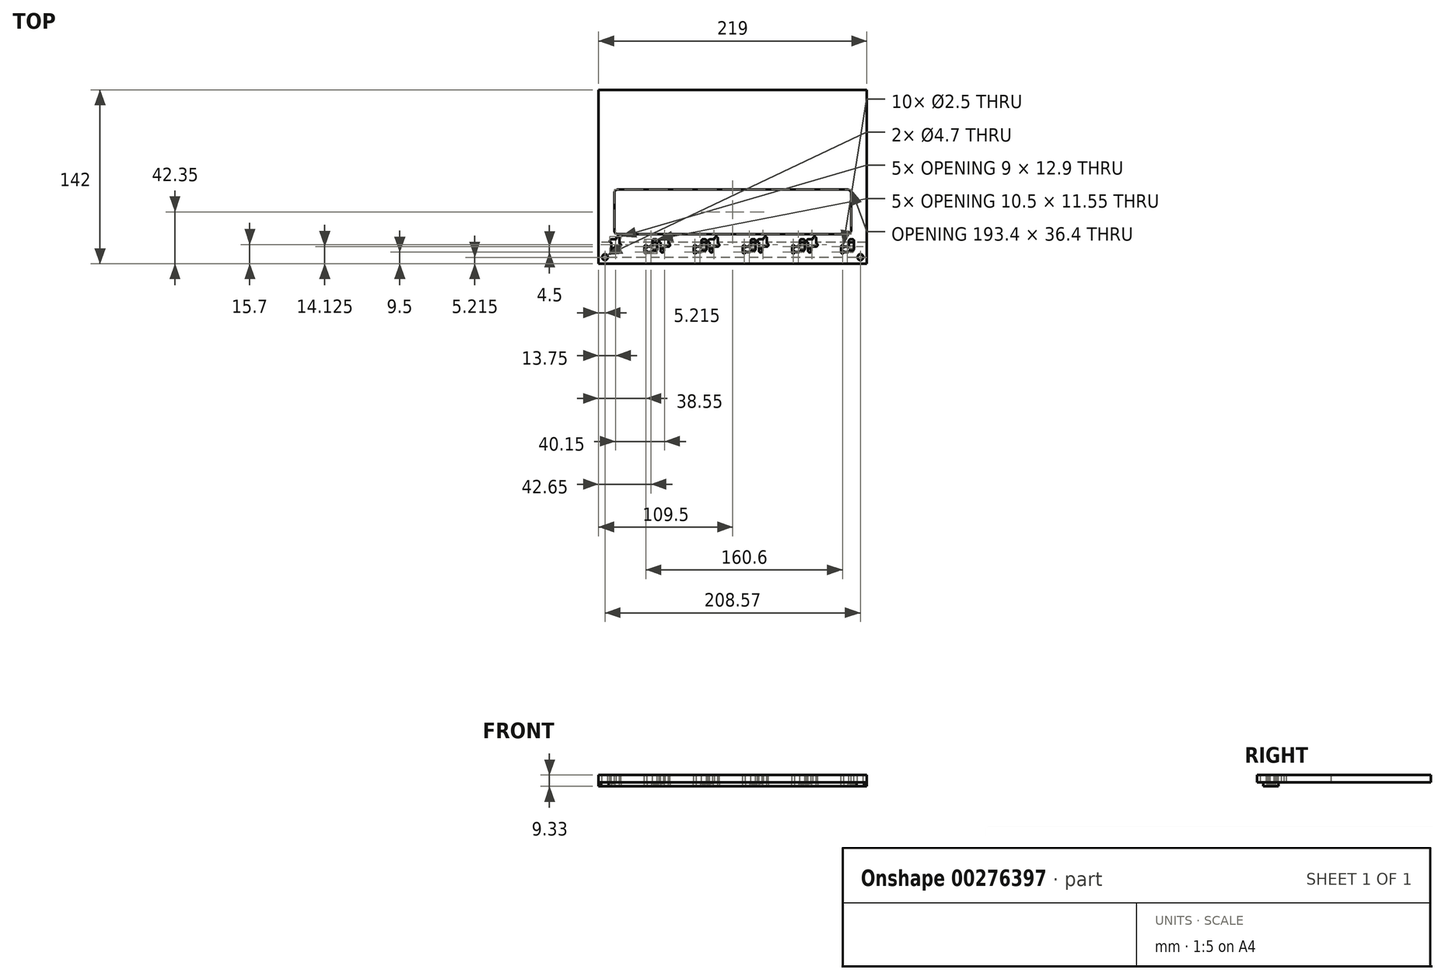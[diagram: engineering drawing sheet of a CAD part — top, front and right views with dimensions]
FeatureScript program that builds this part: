
annotation { "Feature Type Name" : "Feature", "Feature Type Description" : "" }
export const myFeature = defineFeature(function(context is Context, id is Id, definition is map)
    precondition{}
    {
        {
            var Q0;
            Q0=qCreatedBy(makeId("Top.planeOp"),FACE);
            var sketch = newSketch(context, id + "F0", { "sketchPlane" : qUnion([Q0])});
            skLineSegment(sketch, "E0.bottom", {"start": v(0, 0) * mm, "end": v(219, 0) * mm});
            skLineSegment(sketch, "E0.top", {"start": v(0, 142) * mm, "end": v(219, 142) * mm});
            skLineSegment(sketch, "E0.left", {"start": v(0, 0) * mm, "end": v(0, 142) * mm});
            skLineSegment(sketch, "E0.right", {"start": v(219, 0) * mm, "end": v(219, 142) * mm});
            skSolve(sketch);
        }
        {
            var Q0;
            Q0 = qSketchRegion(id + "F0", true);
            extrude(context, id + "F1", {"entities" : qUnion([Q0]), "depth" : 6.15 * mm});
        }
        {
            var Q0;
            Q0=makeQuery(id+"F1.opExtrude","CAP_FACE",FACE,{"disambiguationData":[OSD([sQuery(id+"F0.wireOp",EDGE,"E0.bottom"),sQuery(id+"F0.wireOp",EDGE,"E0.top"),sQuery(id+"F0.wireOp",EDGE,"E0.left"),sQuery(id+"F0.wireOp",EDGE,"E0.right")])],"isStart":false});
            var sketch = newSketch(context, id + "F2", { "sketchPlane" : qUnion([Q0])});
            skLineSegment(sketch, "E1.bottom", {"start": v(207.5, 19.9) * mm, "end": v(205.5, 19.9) * mm});
            skLineSegment(sketch, "E1.top", {"start": v(207.5, 10.8) * mm, "end": v(204.5, 10.8) * mm});
            skLineSegment(sketch, "E1.left", {"start": v(208.5, 18.9) * mm, "end": v(208.5, 11.8) * mm});
            skLineSegment(sketch, "E1.right", {"start": v(204.5, 18.9) * mm, "end": v(204.5, 14.8) * mm});
            skLineSegment(sketch, "E2.bottom", {"start": v(203.7, 14) * mm, "end": v(200.3, 14) * mm});
            skLineSegment(sketch, "E2.top", {"start": v(203.5, 9.5) * mm, "end": v(200.3, 9.5) * mm});
            skLineSegment(sketch, "E2.left", {"start": v(204.5, 10.8) * mm, "end": v(204.5, 10.5) * mm});
            skLineSegment(sketch, "E2.right", {"start": v(198, 14) * mm, "end": v(198, 9.5) * mm});
            skArc(sketch, "E3", {"start": v(200.3, 14) * mm, "mid": v(199.15, 15.15) * mm, "end": v(198, 14) * mm});
            skArc(sketch, "E4", {"start": v(198, 9.5) * mm, "mid": v(199.15, 8.35) * mm, "end": v(200.3, 9.5) * mm});
            skPoint(sketch, "E5.visualSharp", {"position": v(204.5, 19.9) * mm});
            skArc(sketch, "E5.filletArc", {"start": v(205.5, 19.9) * mm, "mid": v(204.8, 19.6) * mm, "end": v(204.5, 18.9) * mm});
            skPoint(sketch, "E6.visualSharp", {"position": v(208.5, 19.9) * mm});
            skArc(sketch, "E6.filletArc", {"start": v(208.5, 18.9) * mm, "mid": v(208.2, 19.6) * mm, "end": v(207.5, 19.9) * mm});
            skPoint(sketch, "E7.visualSharp", {"position": v(208.5, 10.8) * mm});
            skArc(sketch, "E7.filletArc", {"start": v(207.5, 10.8) * mm, "mid": v(208.2, 11.1) * mm, "end": v(208.5, 11.8) * mm});
            skPoint(sketch, "E8.visualSharp", {"position": v(204.5, 9.5) * mm});
            skArc(sketch, "E8.filletArc", {"start": v(203.5, 9.5) * mm, "mid": v(204.2, 9.8) * mm, "end": v(204.5, 10.5) * mm});
            skPoint(sketch, "E9.1.0.0", {"position": v(168.35, 10.8) * mm});
            skPoint(sketch, "E9.1.0.1", {"position": v(164.35, 19.9) * mm});
            skLineSegment(sketch, "E9.1.0.2", {"start": v(168.35, 18.9) * mm, "end": v(168.35, 11.8) * mm});
            skPoint(sketch, "E9.1.0.3", {"position": v(168.35, 19.9) * mm});
            skPoint(sketch, "E9.1.0.4", {"position": v(164.35, 9.5) * mm});
            skLineSegment(sketch, "E9.1.0.5", {"start": v(164.35, 18.9) * mm, "end": v(164.35, 14.8) * mm});
            skLineSegment(sketch, "E9.1.0.6", {"start": v(157.85, 14) * mm, "end": v(157.85, 9.5) * mm});
            skLineSegment(sketch, "E9.1.0.7", {"start": v(167.35, 10.8) * mm, "end": v(164.35, 10.8) * mm});
            skLineSegment(sketch, "E9.1.0.8", {"start": v(163.55, 14) * mm, "end": v(160.15, 14) * mm});
            skArc(sketch, "E9.1.0.9", {"start": v(167.35, 10.8) * mm, "mid": v(168.06, 11.1) * mm, "end": v(168.35, 11.8) * mm});
            skArc(sketch, "E9.1.0.10", {"start": v(163.35, 9.5) * mm, "mid": v(164.06, 9.8) * mm, "end": v(164.35, 10.5) * mm});
            skLineSegment(sketch, "E9.1.0.11", {"start": v(167.35, 19.9) * mm, "end": v(165.35, 19.9) * mm});
            skArc(sketch, "E9.1.0.12", {"start": v(165.35, 19.9) * mm, "mid": v(164.64, 19.6) * mm, "end": v(164.35, 18.9) * mm});
            skArc(sketch, "E9.1.0.13", {"start": v(168.35, 18.9) * mm, "mid": v(168.06, 19.6) * mm, "end": v(167.35, 19.9) * mm});
            skArc(sketch, "E9.1.0.14", {"start": v(160.15, 14) * mm, "mid": v(159, 15.15) * mm, "end": v(157.85, 14) * mm});
            skLineSegment(sketch, "E9.1.0.15", {"start": v(163.35, 9.5) * mm, "end": v(160.15, 9.5) * mm});
            skArc(sketch, "E9.1.0.16", {"start": v(157.85, 9.5) * mm, "mid": v(159, 8.35) * mm, "end": v(160.15, 9.5) * mm});
            skPoint(sketch, "E9.2.0.0", {"position": v(128.2, 10.8) * mm});
            skPoint(sketch, "E9.2.0.1", {"position": v(124.2, 19.9) * mm});
            skLineSegment(sketch, "E9.2.0.2", {"start": v(128.2, 18.9) * mm, "end": v(128.2, 11.8) * mm});
            skPoint(sketch, "E9.2.0.3", {"position": v(128.2, 19.9) * mm});
            skPoint(sketch, "E9.2.0.4", {"position": v(124.2, 9.5) * mm});
            skLineSegment(sketch, "E9.2.0.5", {"start": v(124.2, 18.9) * mm, "end": v(124.2, 14.8) * mm});
            skLineSegment(sketch, "E9.2.0.6", {"start": v(117.7, 14) * mm, "end": v(117.7, 9.5) * mm});
            skLineSegment(sketch, "E9.2.0.7", {"start": v(127.2, 10.8) * mm, "end": v(124.2, 10.8) * mm});
            skLineSegment(sketch, "E9.2.0.8", {"start": v(123.4, 14) * mm, "end": v(120, 14) * mm});
            skArc(sketch, "E9.2.0.9", {"start": v(127.2, 10.8) * mm, "mid": v(127.9, 11.1) * mm, "end": v(128.2, 11.8) * mm});
            skArc(sketch, "E9.2.0.10", {"start": v(123.2, 9.5) * mm, "mid": v(123.9, 9.8) * mm, "end": v(124.2, 10.5) * mm});
            skLineSegment(sketch, "E9.2.0.11", {"start": v(127.2, 19.9) * mm, "end": v(125.2, 19.9) * mm});
            skArc(sketch, "E9.2.0.12", {"start": v(125.2, 19.9) * mm, "mid": v(124.5, 19.6) * mm, "end": v(124.2, 18.9) * mm});
            skArc(sketch, "E9.2.0.13", {"start": v(128.2, 18.9) * mm, "mid": v(127.9, 19.6) * mm, "end": v(127.2, 19.9) * mm});
            skArc(sketch, "E9.2.0.14", {"start": v(120, 14) * mm, "mid": v(118.85, 15.15) * mm, "end": v(117.7, 14) * mm});
            skLineSegment(sketch, "E9.2.0.15", {"start": v(123.2, 9.5) * mm, "end": v(120, 9.5) * mm});
            skArc(sketch, "E9.2.0.16", {"start": v(117.7, 9.5) * mm, "mid": v(118.85, 8.35) * mm, "end": v(120, 9.5) * mm});
            skPoint(sketch, "E9.3.0.0", {"position": v(88.05, 10.8) * mm});
            skPoint(sketch, "E9.3.0.1", {"position": v(84.05, 19.9) * mm});
            skLineSegment(sketch, "E9.3.0.2", {"start": v(88.05, 18.9) * mm, "end": v(88.05, 11.8) * mm});
            skPoint(sketch, "E9.3.0.3", {"position": v(88.05, 19.9) * mm});
            skPoint(sketch, "E9.3.0.4", {"position": v(84.05, 9.5) * mm});
            skLineSegment(sketch, "E9.3.0.5", {"start": v(84.05, 18.9) * mm, "end": v(84.05, 14.8) * mm});
            skLineSegment(sketch, "E9.3.0.6", {"start": v(77.55, 14) * mm, "end": v(77.55, 9.5) * mm});
            skLineSegment(sketch, "E9.3.0.7", {"start": v(87.05, 10.8) * mm, "end": v(84.05, 10.8) * mm});
            skLineSegment(sketch, "E9.3.0.8", {"start": v(83.25, 14) * mm, "end": v(79.85, 14) * mm});
            skArc(sketch, "E9.3.0.9", {"start": v(87.05, 10.8) * mm, "mid": v(87.76, 11.1) * mm, "end": v(88.05, 11.8) * mm});
            skArc(sketch, "E9.3.0.10", {"start": v(83.05, 9.5) * mm, "mid": v(83.76, 9.8) * mm, "end": v(84.05, 10.5) * mm});
            skLineSegment(sketch, "E9.3.0.11", {"start": v(87.05, 19.9) * mm, "end": v(85.05, 19.9) * mm});
            skArc(sketch, "E9.3.0.12", {"start": v(85.05, 19.9) * mm, "mid": v(84.34, 19.6) * mm, "end": v(84.05, 18.9) * mm});
            skArc(sketch, "E9.3.0.13", {"start": v(88.05, 18.9) * mm, "mid": v(87.76, 19.6) * mm, "end": v(87.05, 19.9) * mm});
            skArc(sketch, "E9.3.0.14", {"start": v(79.85, 14) * mm, "mid": v(78.7, 15.15) * mm, "end": v(77.55, 14) * mm});
            skLineSegment(sketch, "E9.3.0.15", {"start": v(83.05, 9.5) * mm, "end": v(79.85, 9.5) * mm});
            skArc(sketch, "E9.3.0.16", {"start": v(77.55, 9.5) * mm, "mid": v(78.7, 8.35) * mm, "end": v(79.85, 9.5) * mm});
            skPoint(sketch, "E9.4.0.0", {"position": v(47.9, 10.8) * mm});
            skPoint(sketch, "E9.4.0.1", {"position": v(43.9, 19.9) * mm});
            skLineSegment(sketch, "E9.4.0.2", {"start": v(47.9, 18.9) * mm, "end": v(47.9, 11.8) * mm});
            skPoint(sketch, "E9.4.0.3", {"position": v(47.9, 19.9) * mm});
            skPoint(sketch, "E9.4.0.4", {"position": v(43.9, 9.5) * mm});
            skLineSegment(sketch, "E9.4.0.5", {"start": v(43.9, 18.9) * mm, "end": v(43.9, 14.8) * mm});
            skLineSegment(sketch, "E9.4.0.6", {"start": v(37.4, 14) * mm, "end": v(37.4, 9.5) * mm});
            skLineSegment(sketch, "E9.4.0.7", {"start": v(46.9, 10.8) * mm, "end": v(43.9, 10.8) * mm});
            skLineSegment(sketch, "E9.4.0.8", {"start": v(43.1, 14) * mm, "end": v(39.7, 14) * mm});
            skArc(sketch, "E9.4.0.9", {"start": v(46.9, 10.8) * mm, "mid": v(47.6, 11.1) * mm, "end": v(47.9, 11.8) * mm});
            skArc(sketch, "E9.4.0.10", {"start": v(42.9, 9.5) * mm, "mid": v(43.6, 9.8) * mm, "end": v(43.9, 10.5) * mm});
            skLineSegment(sketch, "E9.4.0.11", {"start": v(46.9, 19.9) * mm, "end": v(44.9, 19.9) * mm});
            skArc(sketch, "E9.4.0.12", {"start": v(44.9, 19.9) * mm, "mid": v(44.2, 19.6) * mm, "end": v(43.9, 18.9) * mm});
            skArc(sketch, "E9.4.0.13", {"start": v(47.9, 18.9) * mm, "mid": v(47.6, 19.6) * mm, "end": v(46.9, 19.9) * mm});
            skArc(sketch, "E9.4.0.14", {"start": v(39.7, 14) * mm, "mid": v(38.55, 15.15) * mm, "end": v(37.4, 14) * mm});
            skLineSegment(sketch, "E9.4.0.15", {"start": v(42.9, 9.5) * mm, "end": v(39.7, 9.5) * mm});
            skArc(sketch, "E9.4.0.16", {"start": v(37.4, 9.5) * mm, "mid": v(38.55, 8.35) * mm, "end": v(39.7, 9.5) * mm});
            skLineSegment(sketch, "E9.direction1", {"start": v(198, 9.5) * mm, "end": v(157.85, 9.5) * mm, "construction": true});
            skPoint(sketch, "E10.visualSharp", {"position": v(204.5, 14) * mm});
            skArc(sketch, "E10.filletArc", {"start": v(203.7, 14) * mm, "mid": v(204.27, 14.23) * mm, "end": v(204.5, 14.8) * mm});
            skLineSegment(sketch, "E11.bottom", {"start": v(15.8, 60.55) * mm, "end": v(203.2, 60.55) * mm});
            skLineSegment(sketch, "E11.top", {"start": v(15.8, 24.15) * mm, "end": v(203.2, 24.15) * mm});
            skLineSegment(sketch, "E11.left", {"start": v(12.8, 57.55) * mm, "end": v(12.8, 27.15) * mm});
            skLineSegment(sketch, "E11.right", {"start": v(206.2, 57.55) * mm, "end": v(206.2, 27.15) * mm});
            skPoint(sketch, "E12.visualSharp", {"position": v(206.2, 60.55) * mm});
            skArc(sketch, "E12.filletArc", {"start": v(206.2, 57.55) * mm, "mid": v(205.32, 59.67) * mm, "end": v(203.2, 60.55) * mm});
            skPoint(sketch, "E13.visualSharp", {"position": v(206.2, 24.15) * mm});
            skArc(sketch, "E13.filletArc", {"start": v(203.2, 24.15) * mm, "mid": v(205.32, 25.03) * mm, "end": v(206.2, 27.15) * mm});
            skPoint(sketch, "E14.visualSharp", {"position": v(12.8, 24.15) * mm});
            skArc(sketch, "E14.filletArc", {"start": v(12.8, 27.15) * mm, "mid": v(13.68, 25.03) * mm, "end": v(15.8, 24.15) * mm});
            skPoint(sketch, "E15.visualSharp", {"position": v(12.8, 60.55) * mm});
            skArc(sketch, "E15.filletArc", {"start": v(15.8, 60.55) * mm, "mid": v(13.68, 59.67) * mm, "end": v(12.8, 57.55) * mm});
            skLineSegment(sketch, "E16.bottom", {"start": v(171.1, 19.9) * mm, "end": v(177.6, 19.9) * mm});
            skLineSegment(sketch, "E16.top", {"start": v(171.1, 14) * mm, "end": v(177.6, 14) * mm});
            skLineSegment(sketch, "E16.left", {"start": v(171.1, 19.9) * mm, "end": v(171.1, 14) * mm});
            skLineSegment(sketch, "E16.right", {"start": v(177.6, 19.9) * mm, "end": v(177.6, 14) * mm});
            skArc(sketch, "E17", {"start": v(171.1, 19.9) * mm, "mid": v(169.85, 18.65) * mm, "end": v(171.1, 17.4) * mm});
            skArc(sketch, "E18", {"start": v(177.6, 14) * mm, "mid": v(178.85, 15.25) * mm, "end": v(177.6, 16.5) * mm});
            skLineSegment(sketch, "E19.bottom", {"start": v(171.1, 14) * mm, "end": v(173.6, 14) * mm});
            skLineSegment(sketch, "E19.top", {"start": v(171.1, 10.5) * mm, "end": v(173.6, 10.5) * mm});
            skLineSegment(sketch, "E19.left", {"start": v(171.1, 14) * mm, "end": v(171.1, 10.5) * mm});
            skLineSegment(sketch, "E19.right", {"start": v(173.6, 14) * mm, "end": v(173.6, 10.5) * mm});
            skArc(sketch, "E20", {"start": v(171.1, 10.5) * mm, "mid": v(172.35, 9.25) * mm, "end": v(173.6, 10.5) * mm});
            skLineSegment(sketch, "E21.bottom", {"start": v(177.6, 19.9) * mm, "end": v(175.1, 19.9) * mm});
            skLineSegment(sketch, "E21.top", {"start": v(177.6, 20.9) * mm, "end": v(175.1, 20.9) * mm});
            skLineSegment(sketch, "E21.left", {"start": v(177.6, 19.9) * mm, "end": v(177.6, 20.9) * mm});
            skLineSegment(sketch, "E21.right", {"start": v(175.1, 19.9) * mm, "end": v(175.1, 20.9) * mm});
            skArc(sketch, "E22", {"start": v(177.6, 20.9) * mm, "mid": v(176.35, 22.15) * mm, "end": v(175.1, 20.9) * mm});
            skArc(sketch, "E23.1.0.0", {"start": v(130.95, 10.5) * mm, "mid": v(132.2, 9.25) * mm, "end": v(133.45, 10.5) * mm});
            skLineSegment(sketch, "E23.1.0.1", {"start": v(137.45, 19.9) * mm, "end": v(137.45, 20.9) * mm});
            skLineSegment(sketch, "E23.1.0.2", {"start": v(130.95, 14) * mm, "end": v(130.95, 10.5) * mm});
            skArc(sketch, "E23.1.0.3", {"start": v(137.45, 14) * mm, "mid": v(138.7, 15.25) * mm, "end": v(137.45, 16.5) * mm});
            skLineSegment(sketch, "E23.1.0.4", {"start": v(133.45, 14) * mm, "end": v(133.45, 10.5) * mm});
            skLineSegment(sketch, "E23.1.0.5", {"start": v(130.95, 10.5) * mm, "end": v(133.45, 10.5) * mm});
            skArc(sketch, "E23.1.0.6", {"start": v(137.45, 20.9) * mm, "mid": v(136.2, 22.15) * mm, "end": v(134.95, 20.9) * mm});
            skArc(sketch, "E23.1.0.7", {"start": v(130.95, 19.9) * mm, "mid": v(129.7, 18.65) * mm, "end": v(130.95, 17.4) * mm});
            skLineSegment(sketch, "E23.1.0.8", {"start": v(130.95, 14) * mm, "end": v(137.45, 14) * mm});
            skLineSegment(sketch, "E23.1.0.9", {"start": v(137.45, 19.9) * mm, "end": v(137.45, 14) * mm});
            skLineSegment(sketch, "E23.1.0.10", {"start": v(134.95, 19.9) * mm, "end": v(134.95, 20.9) * mm});
            skLineSegment(sketch, "E23.1.0.11", {"start": v(137.45, 20.9) * mm, "end": v(134.95, 20.9) * mm});
            skLineSegment(sketch, "E23.1.0.12", {"start": v(130.95, 14) * mm, "end": v(133.45, 14) * mm});
            skLineSegment(sketch, "E23.1.0.13", {"start": v(130.95, 19.9) * mm, "end": v(130.95, 14) * mm});
            skLineSegment(sketch, "E23.1.0.14", {"start": v(137.45, 19.9) * mm, "end": v(134.95, 19.9) * mm});
            skLineSegment(sketch, "E23.1.0.15", {"start": v(130.95, 19.9) * mm, "end": v(137.45, 19.9) * mm});
            skArc(sketch, "E23.2.0.0", {"start": v(90.8, 10.5) * mm, "mid": v(92.05, 9.25) * mm, "end": v(93.3, 10.5) * mm});
            skLineSegment(sketch, "E23.2.0.1", {"start": v(97.3, 19.9) * mm, "end": v(97.3, 20.9) * mm});
            skLineSegment(sketch, "E23.2.0.2", {"start": v(90.8, 14) * mm, "end": v(90.8, 10.5) * mm});
            skArc(sketch, "E23.2.0.3", {"start": v(97.3, 14) * mm, "mid": v(98.55, 15.25) * mm, "end": v(97.3, 16.5) * mm});
            skLineSegment(sketch, "E23.2.0.4", {"start": v(93.3, 14) * mm, "end": v(93.3, 10.5) * mm});
            skLineSegment(sketch, "E23.2.0.5", {"start": v(90.8, 10.5) * mm, "end": v(93.3, 10.5) * mm});
            skArc(sketch, "E23.2.0.6", {"start": v(97.3, 20.9) * mm, "mid": v(96.05, 22.15) * mm, "end": v(94.8, 20.9) * mm});
            skArc(sketch, "E23.2.0.7", {"start": v(90.8, 19.9) * mm, "mid": v(89.55, 18.65) * mm, "end": v(90.8, 17.4) * mm});
            skLineSegment(sketch, "E23.2.0.8", {"start": v(90.8, 14) * mm, "end": v(97.3, 14) * mm});
            skLineSegment(sketch, "E23.2.0.9", {"start": v(97.3, 19.9) * mm, "end": v(97.3, 14) * mm});
            skLineSegment(sketch, "E23.2.0.10", {"start": v(94.8, 19.9) * mm, "end": v(94.8, 20.9) * mm});
            skLineSegment(sketch, "E23.2.0.11", {"start": v(97.3, 20.9) * mm, "end": v(94.8, 20.9) * mm});
            skLineSegment(sketch, "E23.2.0.12", {"start": v(90.8, 14) * mm, "end": v(93.3, 14) * mm});
            skLineSegment(sketch, "E23.2.0.13", {"start": v(90.8, 19.9) * mm, "end": v(90.8, 14) * mm});
            skLineSegment(sketch, "E23.2.0.14", {"start": v(97.3, 19.9) * mm, "end": v(94.8, 19.9) * mm});
            skLineSegment(sketch, "E23.2.0.15", {"start": v(90.8, 19.9) * mm, "end": v(97.3, 19.9) * mm});
            skArc(sketch, "E23.3.0.0", {"start": v(50.65, 10.5) * mm, "mid": v(51.9, 9.25) * mm, "end": v(53.15, 10.5) * mm});
            skLineSegment(sketch, "E23.3.0.1", {"start": v(57.15, 19.9) * mm, "end": v(57.15, 20.9) * mm});
            skLineSegment(sketch, "E23.3.0.2", {"start": v(50.65, 14) * mm, "end": v(50.65, 10.5) * mm});
            skArc(sketch, "E23.3.0.3", {"start": v(57.15, 14) * mm, "mid": v(58.4, 15.25) * mm, "end": v(57.15, 16.5) * mm});
            skLineSegment(sketch, "E23.3.0.4", {"start": v(53.15, 14) * mm, "end": v(53.15, 10.5) * mm});
            skLineSegment(sketch, "E23.3.0.5", {"start": v(50.65, 10.5) * mm, "end": v(53.15, 10.5) * mm});
            skArc(sketch, "E23.3.0.6", {"start": v(57.15, 20.9) * mm, "mid": v(55.9, 22.15) * mm, "end": v(54.65, 20.9) * mm});
            skArc(sketch, "E23.3.0.7", {"start": v(50.65, 19.9) * mm, "mid": v(49.4, 18.65) * mm, "end": v(50.65, 17.4) * mm});
            skLineSegment(sketch, "E23.3.0.8", {"start": v(50.65, 14) * mm, "end": v(57.15, 14) * mm});
            skLineSegment(sketch, "E23.3.0.9", {"start": v(57.15, 19.9) * mm, "end": v(57.15, 14) * mm});
            skLineSegment(sketch, "E23.3.0.10", {"start": v(54.65, 19.9) * mm, "end": v(54.65, 20.9) * mm});
            skLineSegment(sketch, "E23.3.0.11", {"start": v(57.15, 20.9) * mm, "end": v(54.65, 20.9) * mm});
            skLineSegment(sketch, "E23.3.0.12", {"start": v(50.65, 14) * mm, "end": v(53.15, 14) * mm});
            skLineSegment(sketch, "E23.3.0.13", {"start": v(50.65, 19.9) * mm, "end": v(50.65, 14) * mm});
            skLineSegment(sketch, "E23.3.0.14", {"start": v(57.15, 19.9) * mm, "end": v(54.65, 19.9) * mm});
            skLineSegment(sketch, "E23.3.0.15", {"start": v(50.65, 19.9) * mm, "end": v(57.15, 19.9) * mm});
            skArc(sketch, "E23.4.0.0", {"start": v(10.5, 10.5) * mm, "mid": v(11.75, 9.25) * mm, "end": v(13, 10.5) * mm});
            skLineSegment(sketch, "E23.4.0.1", {"start": v(17, 19.9) * mm, "end": v(17, 20.9) * mm});
            skLineSegment(sketch, "E23.4.0.2", {"start": v(10.5, 14) * mm, "end": v(10.5, 10.5) * mm});
            skArc(sketch, "E23.4.0.3", {"start": v(17, 14) * mm, "mid": v(18.25, 15.25) * mm, "end": v(17, 16.5) * mm});
            skLineSegment(sketch, "E23.4.0.4", {"start": v(13, 14) * mm, "end": v(13, 10.5) * mm});
            skLineSegment(sketch, "E23.4.0.5", {"start": v(10.5, 10.5) * mm, "end": v(13, 10.5) * mm});
            skArc(sketch, "E23.4.0.6", {"start": v(17, 20.9) * mm, "mid": v(15.75, 22.15) * mm, "end": v(14.5, 20.9) * mm});
            skArc(sketch, "E23.4.0.7", {"start": v(10.5, 19.9) * mm, "mid": v(9.25, 18.65) * mm, "end": v(10.5, 17.4) * mm});
            skLineSegment(sketch, "E23.4.0.8", {"start": v(10.5, 14) * mm, "end": v(17, 14) * mm});
            skLineSegment(sketch, "E23.4.0.9", {"start": v(17, 19.9) * mm, "end": v(17, 14) * mm});
            skLineSegment(sketch, "E23.4.0.10", {"start": v(14.5, 19.9) * mm, "end": v(14.5, 20.9) * mm});
            skLineSegment(sketch, "E23.4.0.11", {"start": v(17, 20.9) * mm, "end": v(14.5, 20.9) * mm});
            skLineSegment(sketch, "E23.4.0.12", {"start": v(10.5, 14) * mm, "end": v(13, 14) * mm});
            skLineSegment(sketch, "E23.4.0.13", {"start": v(10.5, 19.9) * mm, "end": v(10.5, 14) * mm});
            skLineSegment(sketch, "E23.4.0.14", {"start": v(17, 19.9) * mm, "end": v(14.5, 19.9) * mm});
            skLineSegment(sketch, "E23.4.0.15", {"start": v(10.5, 19.9) * mm, "end": v(17, 19.9) * mm});
            skLineSegment(sketch, "E23.direction1", {"start": v(171.1, 10.5) * mm, "end": v(130.95, 10.5) * mm, "construction": true});
            skPoint(sketch, "E24.visualSharp", {"position": v(164.35, 14) * mm});
            skArc(sketch, "E24.filletArc", {"start": v(163.55, 14) * mm, "mid": v(164.12, 14.23) * mm, "end": v(164.35, 14.8) * mm});
            skPoint(sketch, "E25.visualSharp", {"position": v(124.2, 14) * mm});
            skArc(sketch, "E25.filletArc", {"start": v(123.4, 14) * mm, "mid": v(123.97, 14.23) * mm, "end": v(124.2, 14.8) * mm});
            skPoint(sketch, "E26.visualSharp", {"position": v(84.05, 14) * mm});
            skArc(sketch, "E26.filletArc", {"start": v(83.25, 14) * mm, "mid": v(83.82, 14.23) * mm, "end": v(84.05, 14.8) * mm});
            skPoint(sketch, "E27.visualSharp", {"position": v(43.9, 14) * mm});
            skArc(sketch, "E27.filletArc", {"start": v(43.1, 14) * mm, "mid": v(43.67, 14.23) * mm, "end": v(43.9, 14.8) * mm});
            skCircle(sketch, "E28", {"center": v(213.78, 5.21) * mm, "radius": 2.35 * mm});
            skCircle(sketch, "E29", {"center": v(5.21, 5.21) * mm, "radius": 2.35 * mm});
            skLineSegment(sketch, "E30", {"start": v(164.35, 10.5) * mm, "end": v(164.35, 10.8) * mm});
            skLineSegment(sketch, "E31", {"start": v(124.2, 10.5) * mm, "end": v(124.2, 10.8) * mm});
            skLineSegment(sketch, "E32", {"start": v(84.05, 10.8) * mm, "end": v(84.05, 10.5) * mm});
            skLineSegment(sketch, "E33", {"start": v(43.9, 10.8) * mm, "end": v(43.9, 10.5) * mm});
            skSolve(sketch);
        }
        {
            var Q0;
            Q0 = qSketchRegion(id + "F2", true);
            extrude(context, id + "F3", {"entities" : qUnion([Q0]), "operationType" : NewBodyOperationType.REMOVE, "endBound" : BoundingType.THROUGH_ALL, "oppositeDirection" : true, "depth" : 25 * mm});
        }
        {
            var Q0;
            Q0=makeQuery(id+"F1.opExtrude","CAP_FACE",FACE,{"disambiguationData":[OSD([sQuery(id+"F0.wireOp",EDGE,"E0.bottom"),sQuery(id+"F0.wireOp",EDGE,"E0.top"),sQuery(id+"F0.wireOp",EDGE,"E0.left"),sQuery(id+"F0.wireOp",EDGE,"E0.right")])],"isStart":true});
            var sketch = newSketch(context, id + "F4", { "sketchPlane" : qUnion([Q0])});
            skLineSegment(sketch, "E34.bottom", {"start": v(219, -17.6) * mm, "end": v(177.6, -17.6) * mm});
            skLineSegment(sketch, "E34.top", {"start": v(219, -5) * mm, "end": v(216.78, -5) * mm});
            skLineSegment(sketch, "E34.left", {"start": v(219, -17.6) * mm, "end": v(219, -5) * mm});
            skLineSegment(sketch, "E34.right", {"start": v(0, -17.6) * mm, "end": v(0, -5) * mm});
            skCircle(sketch, "E35", {"center": v(199.15, -14) * mm, "radius": 1.25 * mm});
            skCircle(sketch, "E36", {"center": v(199.15, -9.5) * mm, "radius": 1.25 * mm});
            skLineSegment(sketch, "E37.top", {"start": v(177.6, -13.95) * mm, "end": v(174.28, -13.95) * mm});
            skLineSegment(sketch, "E37.left", {"start": v(177.6, -17.6) * mm, "end": v(177.6, -17.13) * mm});
            skLineSegment(sketch, "E37.right", {"start": v(171.1, -17.6) * mm, "end": v(171.1, -13.95) * mm});
            skCircle(sketch, "E38.1.0.0", {"center": v(159, -14) * mm, "radius": 1.25 * mm});
            skCircle(sketch, "E38.1.0.2", {"center": v(159, -9.5) * mm, "radius": 1.25 * mm});
            skLineSegment(sketch, "E38.1.0.3", {"start": v(137.45, -13.95) * mm, "end": v(134.13, -13.95) * mm});
            skLineSegment(sketch, "E38.1.0.4", {"start": v(137.45, -17.6) * mm, "end": v(137.45, -17.13) * mm});
            skLineSegment(sketch, "E38.1.0.5", {"start": v(130.95, -17.6) * mm, "end": v(130.95, -13.95) * mm});
            skCircle(sketch, "E38.2.0.0", {"center": v(118.85, -14) * mm, "radius": 1.25 * mm});
            skCircle(sketch, "E38.2.0.2", {"center": v(118.85, -9.5) * mm, "radius": 1.25 * mm});
            skLineSegment(sketch, "E38.2.0.3", {"start": v(97.3, -13.95) * mm, "end": v(93.98, -13.95) * mm});
            skLineSegment(sketch, "E38.2.0.4", {"start": v(97.3, -17.6) * mm, "end": v(97.3, -17.13) * mm});
            skLineSegment(sketch, "E38.2.0.5", {"start": v(90.8, -17.6) * mm, "end": v(90.8, -13.95) * mm});
            skCircle(sketch, "E38.3.0.0", {"center": v(78.7, -14) * mm, "radius": 1.25 * mm});
            skCircle(sketch, "E38.3.0.2", {"center": v(78.7, -9.5) * mm, "radius": 1.25 * mm});
            skLineSegment(sketch, "E38.3.0.3", {"start": v(57.15, -13.95) * mm, "end": v(53.83, -13.95) * mm});
            skLineSegment(sketch, "E38.3.0.4", {"start": v(57.15, -17.6) * mm, "end": v(57.15, -17.13) * mm});
            skLineSegment(sketch, "E38.3.0.5", {"start": v(50.65, -17.6) * mm, "end": v(50.65, -13.95) * mm});
            skCircle(sketch, "E38.4.0.0", {"center": v(38.55, -14) * mm, "radius": 1.25 * mm});
            skCircle(sketch, "E38.4.0.2", {"center": v(38.55, -9.5) * mm, "radius": 1.25 * mm});
            skLineSegment(sketch, "E38.4.0.3", {"start": v(17, -13.95) * mm, "end": v(13.68, -13.95) * mm});
            skLineSegment(sketch, "E38.4.0.4", {"start": v(17, -17.6) * mm, "end": v(17, -17.13) * mm});
            skLineSegment(sketch, "E38.4.0.5", {"start": v(10.5, -17.6) * mm, "end": v(10.5, -13.95) * mm});
            skLineSegment(sketch, "E38.direction1", {"start": v(171.1, -17.6) * mm, "end": v(137.45, -17.6) * mm, "construction": true});
            skLineSegment(sketch, "E39.trimOffspring", {"start": v(171.1, -17.6) * mm, "end": v(137.45, -17.6) * mm});
            skLineSegment(sketch, "E40.trimOffspring", {"start": v(130.95, -17.6) * mm, "end": v(97.3, -17.6) * mm});
            skLineSegment(sketch, "E41.trimOffspring", {"start": v(90.8, -17.6) * mm, "end": v(57.15, -17.6) * mm});
            skLineSegment(sketch, "E42.trimOffspring", {"start": v(50.65, -17.6) * mm, "end": v(17, -17.6) * mm});
            skLineSegment(sketch, "E43.trimOffspring", {"start": v(10.5, -17.6) * mm, "end": v(0, -17.6) * mm});
            skArc(sketch, "E44", {"start": v(13.68, -13.95) * mm, "mid": v(12.1, -12.36) * mm, "end": v(10.5, -13.95) * mm});
            skArc(sketch, "E45", {"start": v(17, -17.13) * mm, "mid": v(18.6, -15.54) * mm, "end": v(17, -13.95) * mm});
            skArc(sketch, "E46", {"start": v(174.28, -13.95) * mm, "mid": v(172.7, -12.36) * mm, "end": v(171.1, -13.95) * mm});
            skArc(sketch, "E47", {"start": v(177.6, -17.13) * mm, "mid": v(179.2, -15.54) * mm, "end": v(177.6, -13.95) * mm});
            skArc(sketch, "E48", {"start": v(137.45, -17.13) * mm, "mid": v(139.04, -15.54) * mm, "end": v(137.45, -13.95) * mm});
            skArc(sketch, "E49", {"start": v(134.13, -13.95) * mm, "mid": v(132.54, -12.36) * mm, "end": v(130.95, -13.95) * mm});
            skArc(sketch, "E50", {"start": v(97.3, -17.13) * mm, "mid": v(98.89, -15.54) * mm, "end": v(97.3, -13.95) * mm});
            skArc(sketch, "E51", {"start": v(93.98, -13.95) * mm, "mid": v(92.4, -12.36) * mm, "end": v(90.8, -13.95) * mm});
            skArc(sketch, "E52", {"start": v(57.15, -17.13) * mm, "mid": v(58.74, -15.54) * mm, "end": v(57.15, -13.95) * mm});
            skArc(sketch, "E53", {"start": v(53.83, -13.95) * mm, "mid": v(52.24, -12.36) * mm, "end": v(50.65, -13.95) * mm});
            skArc(sketch, "E54", {"start": v(2.22, -5) * mm, "mid": v(5.21, -8.21) * mm, "end": v(8.2, -5) * mm});
            skLineSegment(sketch, "E55.trimOffspring", {"start": v(2.22, -5) * mm, "end": v(0, -5) * mm});
            skArc(sketch, "E56", {"start": v(210.8, -5) * mm, "mid": v(213.78, -8.21) * mm, "end": v(216.78, -5) * mm});
            skLineSegment(sketch, "E57.trimOffspring", {"start": v(210.8, -5) * mm, "end": v(8.2, -5) * mm});
            skSolve(sketch);
        }
        {
            var Q0;
            Q0 = qSketchRegion(id + "F4", true);
            extrude(context, id + "F5", {"entities" : qUnion([Q0]), "offsetDistance" : 25 * mm, "depth" : 3.17 * mm});
        }
        {
            var Q0;
            Q0=makeQuery(id+"F5.opExtrude","CAP_FACE",FACE,{"disambiguationData":[OSD([sQuery(id+"F4.wireOp",EDGE,"E34.bottom"),sQuery(id+"F4.wireOp",EDGE,"E34.top"),sQuery(id+"F4.wireOp",EDGE,"E34.left"),sQuery(id+"F4.wireOp",EDGE,"E34.right"),sQuery(id+"F4.wireOp",EDGE,"E35"),sQuery(id+"F4.wireOp",EDGE,"E36"),sQuery(id+"F4.wireOp",EDGE,"E37.top"),sQuery(id+"F4.wireOp",EDGE,"E37.left"),sQuery(id+"F4.wireOp",EDGE,"E37.right"),sQuery(id+"F4.wireOp",EDGE,"E38.1.0.0"),sQuery(id+"F4.wireOp",EDGE,"E38.1.0.2"),sQuery(id+"F4.wireOp",EDGE,"E38.1.0.3"),sQuery(id+"F4.wireOp",EDGE,"E38.1.0.4"),sQuery(id+"F4.wireOp",EDGE,"E38.1.0.5"),sQuery(id+"F4.wireOp",EDGE,"E38.2.0.0"),sQuery(id+"F4.wireOp",EDGE,"E38.2.0.2"),sQuery(id+"F4.wireOp",EDGE,"E38.2.0.3"),sQuery(id+"F4.wireOp",EDGE,"E38.2.0.4"),sQuery(id+"F4.wireOp",EDGE,"E38.2.0.5"),sQuery(id+"F4.wireOp",EDGE,"E38.3.0.0"),sQuery(id+"F4.wireOp",EDGE,"E38.3.0.2"),sQuery(id+"F4.wireOp",EDGE,"E38.3.0.3"),sQuery(id+"F4.wireOp",EDGE,"E38.3.0.4"),sQuery(id+"F4.wireOp",EDGE,"E38.3.0.5"),sQuery(id+"F4.wireOp",EDGE,"E38.4.0.0"),sQuery(id+"F4.wireOp",EDGE,"E38.4.0.2"),sQuery(id+"F4.wireOp",EDGE,"E38.4.0.3"),sQuery(id+"F4.wireOp",EDGE,"E38.4.0.4"),sQuery(id+"F4.wireOp",EDGE,"E38.4.0.5"),sQuery(id+"F4.wireOp",EDGE,"E39.trimOffspring"),sQuery(id+"F4.wireOp",EDGE,"E40.trimOffspring"),sQuery(id+"F4.wireOp",EDGE,"E41.trimOffspring"),sQuery(id+"F4.wireOp",EDGE,"E42.trimOffspring"),sQuery(id+"F4.wireOp",EDGE,"E43.trimOffspring")])],"isStart":false});
            var sketch = newSketch(context, id + "F6", { "sketchPlane" : qUnion([Q0])});
            skLineSegment(sketch, "E58.bottom", {"start": v(208.5, -14.4) * mm, "end": v(204.5, -14.4) * mm});
            skLineSegment(sketch, "E58.top", {"start": v(208.5, -12.5) * mm, "end": v(204.5, -12.5) * mm});
            skLineSegment(sketch, "E58.left", {"start": v(208.5, -14.4) * mm, "end": v(208.5, -12.5) * mm});
            skLineSegment(sketch, "E58.right", {"start": v(204.5, -14.4) * mm, "end": v(204.5, -12.5) * mm});
            skArc(sketch, "E59", {"start": v(204.5, -12.5) * mm, "mid": v(203.55, -13.45) * mm, "end": v(204.5, -14.4) * mm});
            skArc(sketch, "E60", {"start": v(208.5, -14.4) * mm, "mid": v(209.45, -13.45) * mm, "end": v(208.5, -12.5) * mm});
            skLineSegment(sketch, "E61.1.0.0", {"start": v(168.35, -14.4) * mm, "end": v(168.35, -12.5) * mm});
            skLineSegment(sketch, "E61.1.0.1", {"start": v(168.35, -12.5) * mm, "end": v(164.35, -12.5) * mm});
            skArc(sketch, "E61.1.0.2", {"start": v(168.35, -14.4) * mm, "mid": v(169.3, -13.45) * mm, "end": v(168.35, -12.5) * mm});
            skLineSegment(sketch, "E61.1.0.3", {"start": v(164.35, -14.4) * mm, "end": v(164.35, -12.5) * mm});
            skArc(sketch, "E61.1.0.4", {"start": v(164.35, -12.5) * mm, "mid": v(163.4, -13.45) * mm, "end": v(164.35, -14.4) * mm});
            skLineSegment(sketch, "E61.1.0.5", {"start": v(168.35, -14.4) * mm, "end": v(164.35, -14.4) * mm});
            skLineSegment(sketch, "E61.2.0.0", {"start": v(128.2, -14.4) * mm, "end": v(128.2, -12.5) * mm});
            skLineSegment(sketch, "E61.2.0.1", {"start": v(128.2, -12.5) * mm, "end": v(124.2, -12.5) * mm});
            skArc(sketch, "E61.2.0.2", {"start": v(128.2, -14.4) * mm, "mid": v(129.15, -13.45) * mm, "end": v(128.2, -12.5) * mm});
            skLineSegment(sketch, "E61.2.0.3", {"start": v(124.2, -14.4) * mm, "end": v(124.2, -12.5) * mm});
            skArc(sketch, "E61.2.0.4", {"start": v(124.2, -12.5) * mm, "mid": v(123.25, -13.45) * mm, "end": v(124.2, -14.4) * mm});
            skLineSegment(sketch, "E61.2.0.5", {"start": v(128.2, -14.4) * mm, "end": v(124.2, -14.4) * mm});
            skLineSegment(sketch, "E61.3.0.0", {"start": v(88.05, -14.4) * mm, "end": v(88.05, -12.5) * mm});
            skLineSegment(sketch, "E61.3.0.1", {"start": v(88.05, -12.5) * mm, "end": v(84.05, -12.5) * mm});
            skArc(sketch, "E61.3.0.2", {"start": v(88.05, -14.4) * mm, "mid": v(89, -13.45) * mm, "end": v(88.05, -12.5) * mm});
            skLineSegment(sketch, "E61.3.0.3", {"start": v(84.05, -14.4) * mm, "end": v(84.05, -12.5) * mm});
            skArc(sketch, "E61.3.0.4", {"start": v(84.05, -12.5) * mm, "mid": v(83.1, -13.45) * mm, "end": v(84.05, -14.4) * mm});
            skLineSegment(sketch, "E61.3.0.5", {"start": v(88.05, -14.4) * mm, "end": v(84.05, -14.4) * mm});
            skLineSegment(sketch, "E61.4.0.0", {"start": v(47.9, -14.4) * mm, "end": v(47.9, -12.5) * mm});
            skLineSegment(sketch, "E61.4.0.1", {"start": v(47.9, -12.5) * mm, "end": v(43.9, -12.5) * mm});
            skArc(sketch, "E61.4.0.2", {"start": v(47.9, -14.4) * mm, "mid": v(48.85, -13.45) * mm, "end": v(47.9, -12.5) * mm});
            skLineSegment(sketch, "E61.4.0.3", {"start": v(43.9, -14.4) * mm, "end": v(43.9, -12.5) * mm});
            skArc(sketch, "E61.4.0.4", {"start": v(43.9, -12.5) * mm, "mid": v(42.95, -13.45) * mm, "end": v(43.9, -14.4) * mm});
            skLineSegment(sketch, "E61.4.0.5", {"start": v(47.9, -14.4) * mm, "end": v(43.9, -14.4) * mm});
            skLineSegment(sketch, "E61.direction1", {"start": v(204.5, -14.4) * mm, "end": v(164.35, -14.4) * mm, "construction": true});
            skLineSegment(sketch, "E62.bottom", {"start": v(10.5, -13.95) * mm, "end": v(13.68, -13.95) * mm});
            skLineSegment(sketch, "E62.top", {"start": v(10.5, -10.45) * mm, "end": v(13.68, -10.45) * mm});
            skLineSegment(sketch, "E62.left", {"start": v(10.5, -13.95) * mm, "end": v(10.5, -10.45) * mm});
            skLineSegment(sketch, "E62.right", {"start": v(13.68, -13.95) * mm, "end": v(13.68, -10.45) * mm});
            skArc(sketch, "E63", {"start": v(13.68, -10.45) * mm, "mid": v(12.1, -8.86) * mm, "end": v(10.5, -10.45) * mm});
            skLineSegment(sketch, "E64.1.0.0", {"start": v(50.65, -13.95) * mm, "end": v(53.83, -13.95) * mm});
            skLineSegment(sketch, "E64.1.0.1", {"start": v(53.83, -13.95) * mm, "end": v(53.83, -10.45) * mm});
            skLineSegment(sketch, "E64.1.0.2", {"start": v(50.65, -13.95) * mm, "end": v(50.65, -10.45) * mm});
            skArc(sketch, "E64.1.0.3", {"start": v(53.83, -10.45) * mm, "mid": v(52.24, -8.86) * mm, "end": v(50.65, -10.45) * mm});
            skLineSegment(sketch, "E64.1.0.4", {"start": v(50.65, -10.45) * mm, "end": v(53.83, -10.45) * mm});
            skLineSegment(sketch, "E64.2.0.0", {"start": v(90.8, -13.95) * mm, "end": v(93.98, -13.95) * mm});
            skLineSegment(sketch, "E64.2.0.1", {"start": v(93.98, -13.95) * mm, "end": v(93.98, -10.45) * mm});
            skLineSegment(sketch, "E64.2.0.2", {"start": v(90.8, -13.95) * mm, "end": v(90.8, -10.45) * mm});
            skArc(sketch, "E64.2.0.3", {"start": v(93.98, -10.45) * mm, "mid": v(92.4, -8.86) * mm, "end": v(90.8, -10.45) * mm});
            skLineSegment(sketch, "E64.2.0.4", {"start": v(90.8, -10.45) * mm, "end": v(93.98, -10.45) * mm});
            skLineSegment(sketch, "E64.3.0.0", {"start": v(130.95, -13.95) * mm, "end": v(134.13, -13.95) * mm});
            skLineSegment(sketch, "E64.3.0.1", {"start": v(134.13, -13.95) * mm, "end": v(134.13, -10.45) * mm});
            skLineSegment(sketch, "E64.3.0.2", {"start": v(130.95, -13.95) * mm, "end": v(130.95, -10.45) * mm});
            skArc(sketch, "E64.3.0.3", {"start": v(134.13, -10.45) * mm, "mid": v(132.54, -8.86) * mm, "end": v(130.95, -10.45) * mm});
            skLineSegment(sketch, "E64.3.0.4", {"start": v(130.95, -10.45) * mm, "end": v(134.13, -10.45) * mm});
            skLineSegment(sketch, "E64.4.0.0", {"start": v(171.1, -13.95) * mm, "end": v(174.28, -13.95) * mm});
            skLineSegment(sketch, "E64.4.0.1", {"start": v(174.28, -13.95) * mm, "end": v(174.28, -10.45) * mm});
            skLineSegment(sketch, "E64.4.0.2", {"start": v(171.1, -13.95) * mm, "end": v(171.1, -10.45) * mm});
            skArc(sketch, "E64.4.0.3", {"start": v(174.28, -10.45) * mm, "mid": v(172.7, -8.86) * mm, "end": v(171.1, -10.45) * mm});
            skLineSegment(sketch, "E64.4.0.4", {"start": v(171.1, -10.45) * mm, "end": v(174.28, -10.45) * mm});
            skLineSegment(sketch, "E64.direction1", {"start": v(10.5, -13.95) * mm, "end": v(50.65, -13.95) * mm, "construction": true});
            skSolve(sketch);
        }
        {
            var Q0;
            Q0 = qSketchRegion(id + "F6", true);
            extrude(context, id + "F7", {"entities" : qUnion([Q0]), "operationType" : NewBodyOperationType.REMOVE, "oppositeDirection" : true, "depth" : 2.1 * mm});
        }
        {
            var Q0;
            Q0=makeQuery(id+"F5.opExtrude","CAP_FACE",FACE,{"disambiguationData":[OSD([sQuery(id+"F4.wireOp",EDGE,"E34.bottom"),sQuery(id+"F4.wireOp",EDGE,"E34.top"),sQuery(id+"F4.wireOp",EDGE,"E34.left"),sQuery(id+"F4.wireOp",EDGE,"E34.right"),sQuery(id+"F4.wireOp",EDGE,"E35"),sQuery(id+"F4.wireOp",EDGE,"E36"),sQuery(id+"F4.wireOp",EDGE,"E37.top"),sQuery(id+"F4.wireOp",EDGE,"E37.left"),sQuery(id+"F4.wireOp",EDGE,"E37.right"),sQuery(id+"F4.wireOp",EDGE,"E38.1.0.0"),sQuery(id+"F4.wireOp",EDGE,"E38.1.0.2"),sQuery(id+"F4.wireOp",EDGE,"E38.1.0.3"),sQuery(id+"F4.wireOp",EDGE,"E38.1.0.4"),sQuery(id+"F4.wireOp",EDGE,"E38.1.0.5"),sQuery(id+"F4.wireOp",EDGE,"E38.2.0.0"),sQuery(id+"F4.wireOp",EDGE,"E38.2.0.2"),sQuery(id+"F4.wireOp",EDGE,"E38.2.0.3"),sQuery(id+"F4.wireOp",EDGE,"E38.2.0.4"),sQuery(id+"F4.wireOp",EDGE,"E38.2.0.5"),sQuery(id+"F4.wireOp",EDGE,"E38.3.0.0"),sQuery(id+"F4.wireOp",EDGE,"E38.3.0.2"),sQuery(id+"F4.wireOp",EDGE,"E38.3.0.3"),sQuery(id+"F4.wireOp",EDGE,"E38.3.0.4"),sQuery(id+"F4.wireOp",EDGE,"E38.3.0.5"),sQuery(id+"F4.wireOp",EDGE,"E38.4.0.0"),sQuery(id+"F4.wireOp",EDGE,"E38.4.0.2"),sQuery(id+"F4.wireOp",EDGE,"E38.4.0.3"),sQuery(id+"F4.wireOp",EDGE,"E38.4.0.4"),sQuery(id+"F4.wireOp",EDGE,"E38.4.0.5"),sQuery(id+"F4.wireOp",EDGE,"E39.trimOffspring"),sQuery(id+"F4.wireOp",EDGE,"E40.trimOffspring"),sQuery(id+"F4.wireOp",EDGE,"E41.trimOffspring"),sQuery(id+"F4.wireOp",EDGE,"E42.trimOffspring"),sQuery(id+"F4.wireOp",EDGE,"E43.trimOffspring")])],"isStart":false});
            var sketch = newSketch(context, id + "F8", { "sketchPlane" : qUnion([Q0])});
            skLineSegment(sketch, "E65.top", {"start": v(208.1, -17.8) * mm, "end": v(204.91, -17.8) * mm});
            skLineSegment(sketch, "E65.left", {"start": v(208.1, -14.4) * mm, "end": v(208.1, -17.8) * mm});
            skLineSegment(sketch, "E65.right", {"start": v(204.9, -14.4) * mm, "end": v(204.9, -17.8) * mm});
            skLineSegment(sketch, "E66.1.0.0", {"start": v(167.94, -12.68) * mm, "end": v(164.76, -12.68) * mm});
            skLineSegment(sketch, "E66.1.0.1", {"start": v(164.76, -14.4) * mm, "end": v(164.76, -17.8) * mm});
            skLineSegment(sketch, "E66.1.0.2", {"start": v(167.94, -14.4) * mm, "end": v(167.94, -17.8) * mm});
            skLineSegment(sketch, "E66.1.0.3", {"start": v(167.94, -17.8) * mm, "end": v(164.76, -17.8) * mm});
            skLineSegment(sketch, "E66.1.0.4", {"start": v(167.94, -14.4) * mm, "end": v(164.76, -14.4) * mm});
            skLineSegment(sketch, "E66.1.0.5", {"start": v(167.21, -9.5) * mm, "end": v(165.5, -9.5) * mm});
            skLineSegment(sketch, "E66.1.0.6", {"start": v(167.94, -12.68) * mm, "end": v(167.94, -10.23) * mm});
            skLineSegment(sketch, "E66.1.0.7", {"start": v(164.76, -12.68) * mm, "end": v(164.76, -10.23) * mm});
            skLineSegment(sketch, "E66.2.0.0", {"start": v(127.8, -12.68) * mm, "end": v(124.61, -12.68) * mm});
            skLineSegment(sketch, "E66.2.0.1", {"start": v(124.61, -14.4) * mm, "end": v(124.61, -17.8) * mm});
            skLineSegment(sketch, "E66.2.0.2", {"start": v(127.8, -14.4) * mm, "end": v(127.8, -17.8) * mm});
            skLineSegment(sketch, "E66.2.0.3", {"start": v(127.8, -17.8) * mm, "end": v(124.61, -17.8) * mm});
            skLineSegment(sketch, "E66.2.0.4", {"start": v(127.8, -14.4) * mm, "end": v(124.61, -14.4) * mm});
            skLineSegment(sketch, "E66.2.0.5", {"start": v(127.06, -9.5) * mm, "end": v(125.34, -9.5) * mm});
            skLineSegment(sketch, "E66.2.0.6", {"start": v(127.8, -12.68) * mm, "end": v(127.8, -10.23) * mm});
            skLineSegment(sketch, "E66.2.0.7", {"start": v(124.61, -12.68) * mm, "end": v(124.61, -10.23) * mm});
            skLineSegment(sketch, "E66.3.0.0", {"start": v(87.64, -12.68) * mm, "end": v(84.46, -12.68) * mm});
            skLineSegment(sketch, "E66.3.0.1", {"start": v(84.46, -14.4) * mm, "end": v(84.46, -17.8) * mm});
            skLineSegment(sketch, "E66.3.0.2", {"start": v(87.64, -14.4) * mm, "end": v(87.64, -17.8) * mm});
            skLineSegment(sketch, "E66.3.0.3", {"start": v(87.64, -17.8) * mm, "end": v(84.46, -17.8) * mm});
            skLineSegment(sketch, "E66.3.0.4", {"start": v(87.64, -14.4) * mm, "end": v(84.46, -14.4) * mm});
            skLineSegment(sketch, "E66.3.0.5", {"start": v(86.91, -9.5) * mm, "end": v(85.2, -9.5) * mm});
            skLineSegment(sketch, "E66.3.0.6", {"start": v(87.64, -12.68) * mm, "end": v(87.64, -10.23) * mm});
            skLineSegment(sketch, "E66.3.0.7", {"start": v(84.46, -12.68) * mm, "end": v(84.46, -10.23) * mm});
            skLineSegment(sketch, "E66.4.0.0", {"start": v(47.5, -12.68) * mm, "end": v(44.31, -12.68) * mm});
            skLineSegment(sketch, "E66.4.0.1", {"start": v(44.31, -14.4) * mm, "end": v(44.31, -17.8) * mm});
            skLineSegment(sketch, "E66.4.0.2", {"start": v(47.5, -14.4) * mm, "end": v(47.5, -17.8) * mm});
            skLineSegment(sketch, "E66.4.0.3", {"start": v(47.5, -17.8) * mm, "end": v(44.31, -17.8) * mm});
            skLineSegment(sketch, "E66.4.0.4", {"start": v(47.5, -14.4) * mm, "end": v(44.31, -14.4) * mm});
            skLineSegment(sketch, "E66.4.0.5", {"start": v(46.76, -9.5) * mm, "end": v(45.04, -9.5) * mm});
            skLineSegment(sketch, "E66.4.0.6", {"start": v(47.5, -12.68) * mm, "end": v(47.5, -10.23) * mm});
            skLineSegment(sketch, "E66.4.0.7", {"start": v(44.31, -12.68) * mm, "end": v(44.31, -10.23) * mm});
            skLineSegment(sketch, "E66.direction1", {"start": v(204.91, -17.8) * mm, "end": v(164.76, -17.8) * mm, "construction": true});
            skLineSegment(sketch, "E67", {"start": v(204.91, -14.4) * mm, "end": v(208.1, -14.4) * mm});
            skLineSegment(sketch, "E68.bottom", {"start": v(204.91, -12.68) * mm, "end": v(208.1, -12.68) * mm});
            skLineSegment(sketch, "E68.top", {"start": v(205.64, -9.5) * mm, "end": v(207.36, -9.5) * mm});
            skLineSegment(sketch, "E68.left", {"start": v(204.9, -12.68) * mm, "end": v(204.9, -10.23) * mm});
            skLineSegment(sketch, "E68.right", {"start": v(208.1, -12.68) * mm, "end": v(208.1, -10.23) * mm});
            skPoint(sketch, "E69.visualSharp", {"position": v(208.1, -9.5) * mm});
            skArc(sketch, "E69.filletArc", {"start": v(208.1, -10.23) * mm, "mid": v(207.88, -9.71) * mm, "end": v(207.36, -9.5) * mm});
            skPoint(sketch, "E70.visualSharp", {"position": v(204.91, -9.5) * mm});
            skArc(sketch, "E70.filletArc", {"start": v(205.64, -9.5) * mm, "mid": v(205.12, -9.71) * mm, "end": v(204.91, -10.23) * mm});
            skPoint(sketch, "E71.visualSharp", {"position": v(167.94, -9.5) * mm});
            skArc(sketch, "E71.filletArc", {"start": v(167.94, -10.23) * mm, "mid": v(167.73, -9.71) * mm, "end": v(167.21, -9.5) * mm});
            skPoint(sketch, "E72.visualSharp", {"position": v(164.76, -9.5) * mm});
            skArc(sketch, "E72.filletArc", {"start": v(165.5, -9.5) * mm, "mid": v(164.97, -9.71) * mm, "end": v(164.76, -10.23) * mm});
            skPoint(sketch, "E73.visualSharp", {"position": v(127.8, -9.5) * mm});
            skArc(sketch, "E73.filletArc", {"start": v(127.8, -10.23) * mm, "mid": v(127.58, -9.71) * mm, "end": v(127.06, -9.5) * mm});
            skPoint(sketch, "E74.visualSharp", {"position": v(124.61, -9.5) * mm});
            skArc(sketch, "E74.filletArc", {"start": v(125.34, -9.5) * mm, "mid": v(124.82, -9.71) * mm, "end": v(124.61, -10.23) * mm});
            skPoint(sketch, "E75.visualSharp", {"position": v(87.64, -9.5) * mm});
            skArc(sketch, "E75.filletArc", {"start": v(87.64, -10.23) * mm, "mid": v(87.43, -9.71) * mm, "end": v(86.91, -9.5) * mm});
            skPoint(sketch, "E76.visualSharp", {"position": v(84.46, -9.5) * mm});
            skArc(sketch, "E76.filletArc", {"start": v(85.2, -9.5) * mm, "mid": v(84.67, -9.71) * mm, "end": v(84.46, -10.23) * mm});
            skPoint(sketch, "E77.visualSharp", {"position": v(47.5, -9.5) * mm});
            skArc(sketch, "E77.filletArc", {"start": v(47.5, -10.23) * mm, "mid": v(47.28, -9.71) * mm, "end": v(46.76, -9.5) * mm});
            skPoint(sketch, "E78.visualSharp", {"position": v(44.31, -9.5) * mm});
            skArc(sketch, "E78.filletArc", {"start": v(45.04, -9.5) * mm, "mid": v(44.52, -9.71) * mm, "end": v(44.31, -10.23) * mm});
            skSolve(sketch);
        }
        {
            var Q0;
            Q0 = qSketchRegion(id + "F8", true);
            extrude(context, id + "F9", {"entities" : qUnion([Q0]), "operationType" : NewBodyOperationType.REMOVE, "oppositeDirection" : true, "offsetDistance" : 25 * mm, "depth" : 1.1 * mm});
        }
    });
